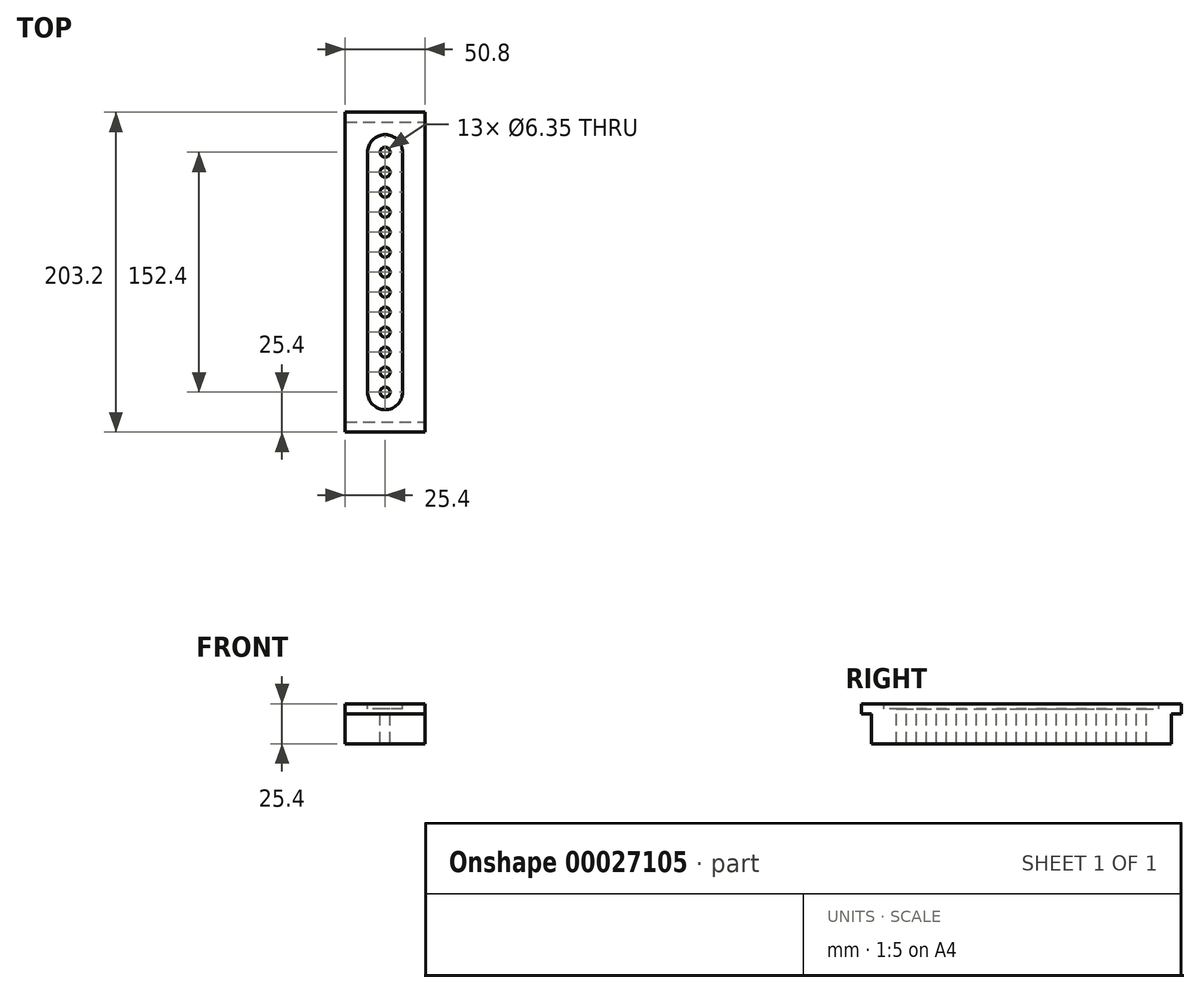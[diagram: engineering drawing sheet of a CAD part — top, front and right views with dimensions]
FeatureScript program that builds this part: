
annotation { "Feature Type Name" : "Feature", "Feature Type Description" : "" }
export const myFeature = defineFeature(function(context is Context, id is Id, definition is map)
    precondition{}
    {
        {
            var Q0;
            Q0=qCreatedBy(makeId("Top.planeOp"),FACE);
            var sketch = newSketch(context, id + "F0", { "sketchPlane" : qUnion([Q0])});
            skLineSegment(sketch, "E0.rect.bottom", {"start": v(-25.4, 101.6) * mm, "end": v(25.4, 101.6) * mm});
            skLineSegment(sketch, "E0.rect.top", {"start": v(-25.4, -101.6) * mm, "end": v(25.4, -101.6) * mm});
            skLineSegment(sketch, "E0.rect.left", {"start": v(-25.4, 101.6) * mm, "end": v(-25.4, -101.6) * mm});
            skLineSegment(sketch, "E0.rect.right", {"start": v(25.4, 101.6) * mm, "end": v(25.4, -101.6) * mm});
            skPoint(sketch, "E0.rect.middle", {"position": v(0, 0) * mm});
            skSolve(sketch);
        }
        {
            var Q0;
            Q0=makeQuery(id+"F0.imprint","IMPRINT",FACE,{"disambiguationData":[TD([[makeQuery(id+"F0.imprint","IMPRINT",EDGE,{"derivedFrom":sQuery(id+"F0.wireOp",EDGE,"E0.rect.bottom")}),-1.0]])]});
            extrude(context, id + "F1", {"entities" : qUnion([Q0]), "depth" : 25.4 * mm});
        }
        {
            var Q0;
            Q0=makeQuery(id+"F1.opExtrude","SWEPT_FACE",FACE,{"disambiguationData":[OSD([sQuery(id+"F0.wireOp",EDGE,"E0.rect.top")])]});
            var sketch = newSketch(context, id + "F2", { "sketchPlane" : qUnion([Q0])});
            skLineSegment(sketch, "E1.bottom", {"start": v(-25.4, 0) * mm, "end": v(25.4, 0) * mm});
            skLineSegment(sketch, "E1.top", {"start": v(-25.4, 0) * mm, "end": v(25.4, 0) * mm});
            skLineSegment(sketch, "E1.left", {"start": v(-25.4, 0) * mm, "end": v(-25.4, 0) * mm});
            skLineSegment(sketch, "E1.right", {"start": v(25.4, 0) * mm, "end": v(25.4, 0) * mm});
            skLineSegment(sketch, "E2.bottom", {"start": v(25.4, 19.05) * mm, "end": v(-25.4, 19.05) * mm});
            skLineSegment(sketch, "E2.top", {"start": v(25.4, 0) * mm, "end": v(-25.4, 0) * mm});
            skLineSegment(sketch, "E2.left", {"start": v(25.4, 19.05) * mm, "end": v(25.4, 0) * mm});
            skLineSegment(sketch, "E2.right", {"start": v(-25.4, 19.05) * mm, "end": v(-25.4, 0) * mm});
            skSolve(sketch);
        }
        {
            var Q0;
            Q0=makeQuery(id+"F2.imprint","IMPRINT",FACE,{"disambiguationData":[TD([[makeQuery(id+"F2.imprint","IMPRINT",EDGE,{"derivedFrom":sQuery(id+"F2.wireOp",EDGE,"E2.bottom")}),1.0]])]});
            extrude(context, id + "F3", {"entities" : qUnion([Q0]), "operationType" : NewBodyOperationType.REMOVE, "oppositeDirection" : true, "depth" : 6.35 * mm});
        }
        {
            var Q0;
            Q0=makeQuery(id+"F1.opExtrude","SWEPT_FACE",FACE,{"disambiguationData":[OSD([sQuery(id+"F0.wireOp",EDGE,"E0.rect.bottom")])]});
            var sketch = newSketch(context, id + "F4", { "sketchPlane" : qUnion([Q0])});
            skLineSegment(sketch, "E3.bottom", {"start": v(-25.4, 0) * mm, "end": v(25.4, 0) * mm});
            skLineSegment(sketch, "E3.top", {"start": v(-25.4, 19.05) * mm, "end": v(25.4, 19.05) * mm});
            skLineSegment(sketch, "E3.left", {"start": v(-25.4, 0) * mm, "end": v(-25.4, 19.05) * mm});
            skLineSegment(sketch, "E3.right", {"start": v(25.4, 0) * mm, "end": v(25.4, 19.05) * mm});
            skSolve(sketch);
        }
        {
            var Q0;
            Q0=makeQuery(id+"F4.imprint","IMPRINT",FACE,{"disambiguationData":[TD([[makeQuery(id+"F4.imprint","IMPRINT",EDGE,{"derivedFrom":sQuery(id+"F4.wireOp",EDGE,"E3.bottom")}),-1.0]])]});
            extrude(context, id + "F5", {"entities" : qUnion([Q0]), "operationType" : NewBodyOperationType.REMOVE, "oppositeDirection" : true, "depth" : 6.35 * mm});
        }
        {
            var Q0;
            Q0=makeQuery(id+"F1.opExtrude","CAP_FACE",FACE,{"disambiguationData":[OSD([sQuery(id+"F0.wireOp",EDGE,"E0.rect.bottom"),sQuery(id+"F0.wireOp",EDGE,"E0.rect.top"),sQuery(id+"F0.wireOp",EDGE,"E0.rect.left"),sQuery(id+"F0.wireOp",EDGE,"E0.rect.right")])],"isStart":false});
            var sketch = newSketch(context, id + "F6", { "sketchPlane" : qUnion([Q0])});
            skLineSegment(sketch, "E4", {"start": v(0, -101.6) * mm, "end": v(0, 101.6) * mm, "construction": true});
            skLineSegment(sketch, "E5", {"start": v(-25.4, 0) * mm, "end": v(25.4, 0) * mm, "construction": true});
            skLineSegment(sketch, "E6.rect.left", {"start": v(-11.11, -76.2) * mm, "end": v(-11.11, 76.2) * mm});
            skLineSegment(sketch, "E6.rect.right", {"start": v(11.11, -76.2) * mm, "end": v(11.11, 76.2) * mm});
            skPoint(sketch, "E6.rect.middle", {"position": v(0, 0) * mm});
            skArc(sketch, "E7", {"start": v(11.11, 76.2) * mm, "mid": v(0, 87.31) * mm, "end": v(-11.11, 76.2) * mm});
            skArc(sketch, "E8", {"start": v(-11.11, -76.2) * mm, "mid": v(0, -87.31) * mm, "end": v(11.11, -76.2) * mm});
            skPoint(sketch, "E9", {"position": v(0, -63.5) * mm});
            skPoint(sketch, "E10", {"position": v(0, -50.8) * mm});
            skPoint(sketch, "E11", {"position": v(0, -38.1) * mm});
            skPoint(sketch, "E12", {"position": v(0, -25.4) * mm});
            skPoint(sketch, "E13", {"position": v(0, -12.7) * mm});
            skPoint(sketch, "E14.MirrorP", {"position": v(0, 12.7) * mm});
            skPoint(sketch, "E15.MirrorP", {"position": v(0, 25.4) * mm});
            skPoint(sketch, "E16.MirrorP", {"position": v(0, 38.1) * mm});
            skPoint(sketch, "E17.MirrorP", {"position": v(0, 50.8) * mm});
            skPoint(sketch, "E18.MirrorP", {"position": v(0, 63.5) * mm});
            skSolve(sketch);
        }
        {
            var Q0;
            Q0=makeQuery(id+"F6.imprint","IMPRINT",FACE,{"disambiguationData":[TD([[makeQuery(id+"F6.imprint","IMPRINT",EDGE,{"derivedFrom":sQuery(id+"F6.wireOp",EDGE,"E6.rect.left")}),-1.0]])]});
            extrude(context, id + "F7", {"entities" : qUnion([Q0]), "operationType" : NewBodyOperationType.REMOVE, "oppositeDirection" : true, "depth" : 3.17 * mm});
        }
        {
            var Q0;
            Q0=sQuery(id+"F6.wireOp",VERTEX,"E8.center");
            var Q1;
            Q1=sQuery(id+"F6.wireOp",VERTEX,"E9");
            var Q2;
            Q2=sQuery(id+"F6.wireOp",VERTEX,"E10");
            var Q3;
            Q3=sQuery(id+"F6.wireOp",VERTEX,"E11");
            var Q4;
            Q4=sQuery(id+"F6.wireOp",VERTEX,"E12");
            var Q5;
            Q5=sQuery(id+"F6.wireOp",VERTEX,"E13");
            var Q6;
            Q6=sQuery(id+"F6.wireOp",VERTEX,"E6.rect.middle");
            var Q7;
            Q7=sQuery(id+"F6.wireOp",VERTEX,"E14.MirrorP");
            var Q8;
            Q8=sQuery(id+"F6.wireOp",VERTEX,"E15.MirrorP");
            var Q9;
            Q9=sQuery(id+"F6.wireOp",VERTEX,"E16.MirrorP");
            var Q10;
            Q10=sQuery(id+"F6.wireOp",VERTEX,"E17.MirrorP");
            var Q11;
            Q11=sQuery(id+"F6.wireOp",VERTEX,"E18.MirrorP");
            var Q12;
            Q12=sQuery(id+"F6.wireOp",VERTEX,"E7.center");
            var Q13;
            Q13=makeQuery(id+"F1.opExtrude","SWEPT_BODY",BODY,{"disambiguationData":[OSD([sQuery(id+"F0.wireOp",EDGE,"E0.rect.bottom"),sQuery(id+"F0.wireOp",EDGE,"E0.rect.top"),sQuery(id+"F0.wireOp",EDGE,"E0.rect.left"),sQuery(id+"F0.wireOp",EDGE,"E0.rect.right")])]});
            hole(context, id + "F8", {"style" : HoleStyle.SIMPLE, "holeDiameter" : 6.35 * mm, "endStyle" : HoleEndStyle.THROUGH, "locations" : qUnion([Q0, Q1, Q2, Q3, Q4, Q5, Q6, Q7, Q8, Q9, Q10, Q11, Q12]), "scope" : qUnion([Q13])});
        }
    });
